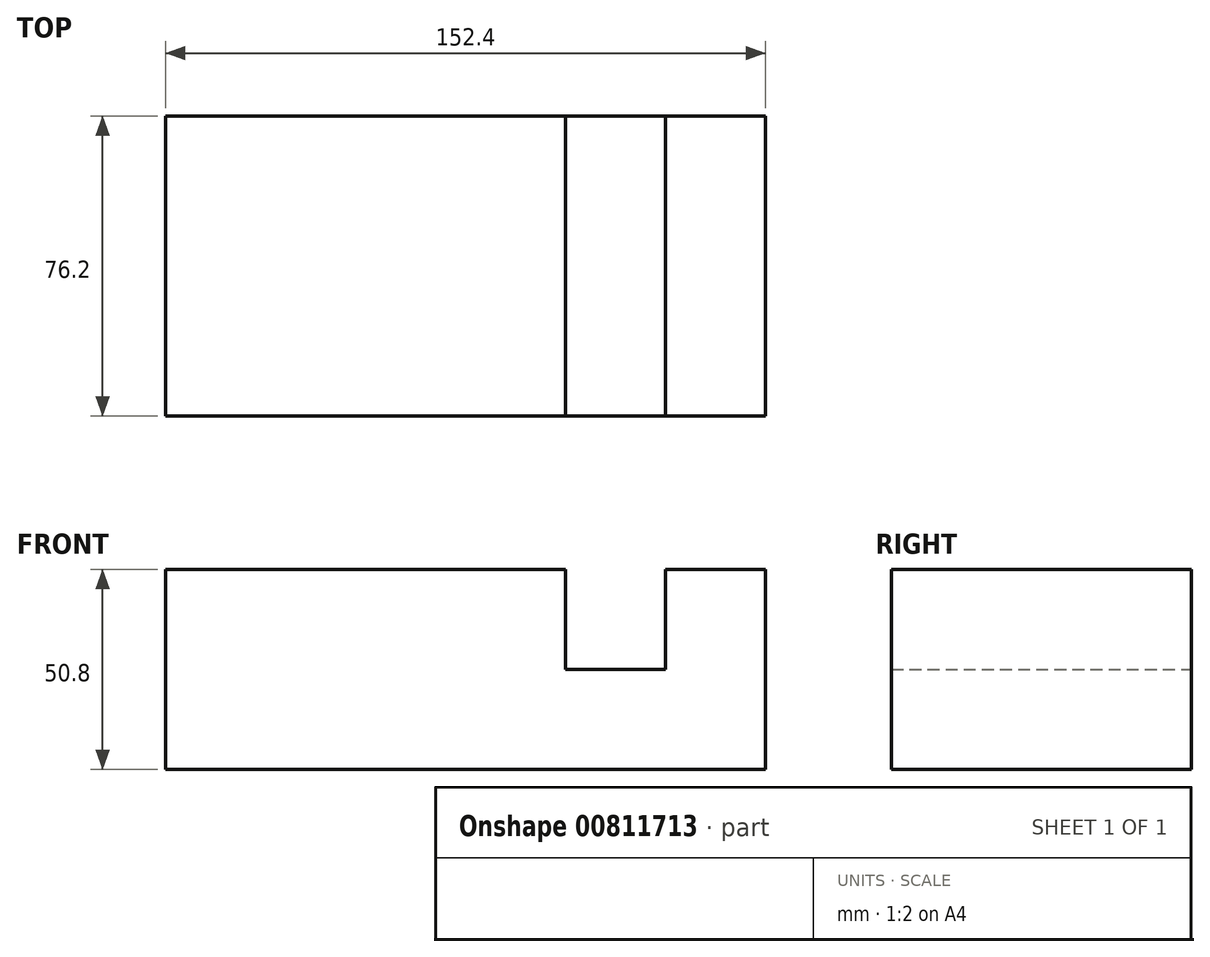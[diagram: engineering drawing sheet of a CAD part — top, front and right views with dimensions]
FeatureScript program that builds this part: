
annotation { "Feature Type Name" : "Feature", "Feature Type Description" : "" }
export const myFeature = defineFeature(function(context is Context, id is Id, definition is map)
    precondition{}
    {
        {
            var Q0;
            Q0=qCreatedBy(makeId("Front.planeOp"),FACE);
            var sketch = newSketch(context, id + "F0", { "sketchPlane" : qUnion([Q0])});
            skLineSegment(sketch, "E0", {"start": v(0, 0) * mm, "end": v(-76.2, 0) * mm});
            skLineSegment(sketch, "E1", {"start": v(0, 0) * mm, "end": v(76.2, 0) * mm});
            skLineSegment(sketch, "E2", {"start": v(76.2, 0) * mm, "end": v(76.2, 50.8) * mm});
            skLineSegment(sketch, "E3", {"start": v(76.2, 50.8) * mm, "end": v(50.8, 50.8) * mm});
            skLineSegment(sketch, "E4", {"start": v(50.8, 50.8) * mm, "end": v(50.8, 25.4) * mm});
            skLineSegment(sketch, "E5", {"start": v(50.8, 25.4) * mm, "end": v(25.4, 25.4) * mm});
            skLineSegment(sketch, "E6", {"start": v(25.4, 25.4) * mm, "end": v(25.4, 50.8) * mm});
            skLineSegment(sketch, "E7", {"start": v(25.4, 50.8) * mm, "end": v(-76.2, 50.8) * mm});
            skLineSegment(sketch, "E8", {"start": v(-76.2, 50.8) * mm, "end": v(-76.2, 0) * mm});
            skSolve(sketch);
        }
        {
            var Q0;
            Q0 = qSketchRegion(id + "F0", true);
            extrude(context, id + "F1", {"entities" : qUnion([Q0]), "depth" : 76.2 * mm, "offsetDistance" : 25.4 * mm});
        }
    });
